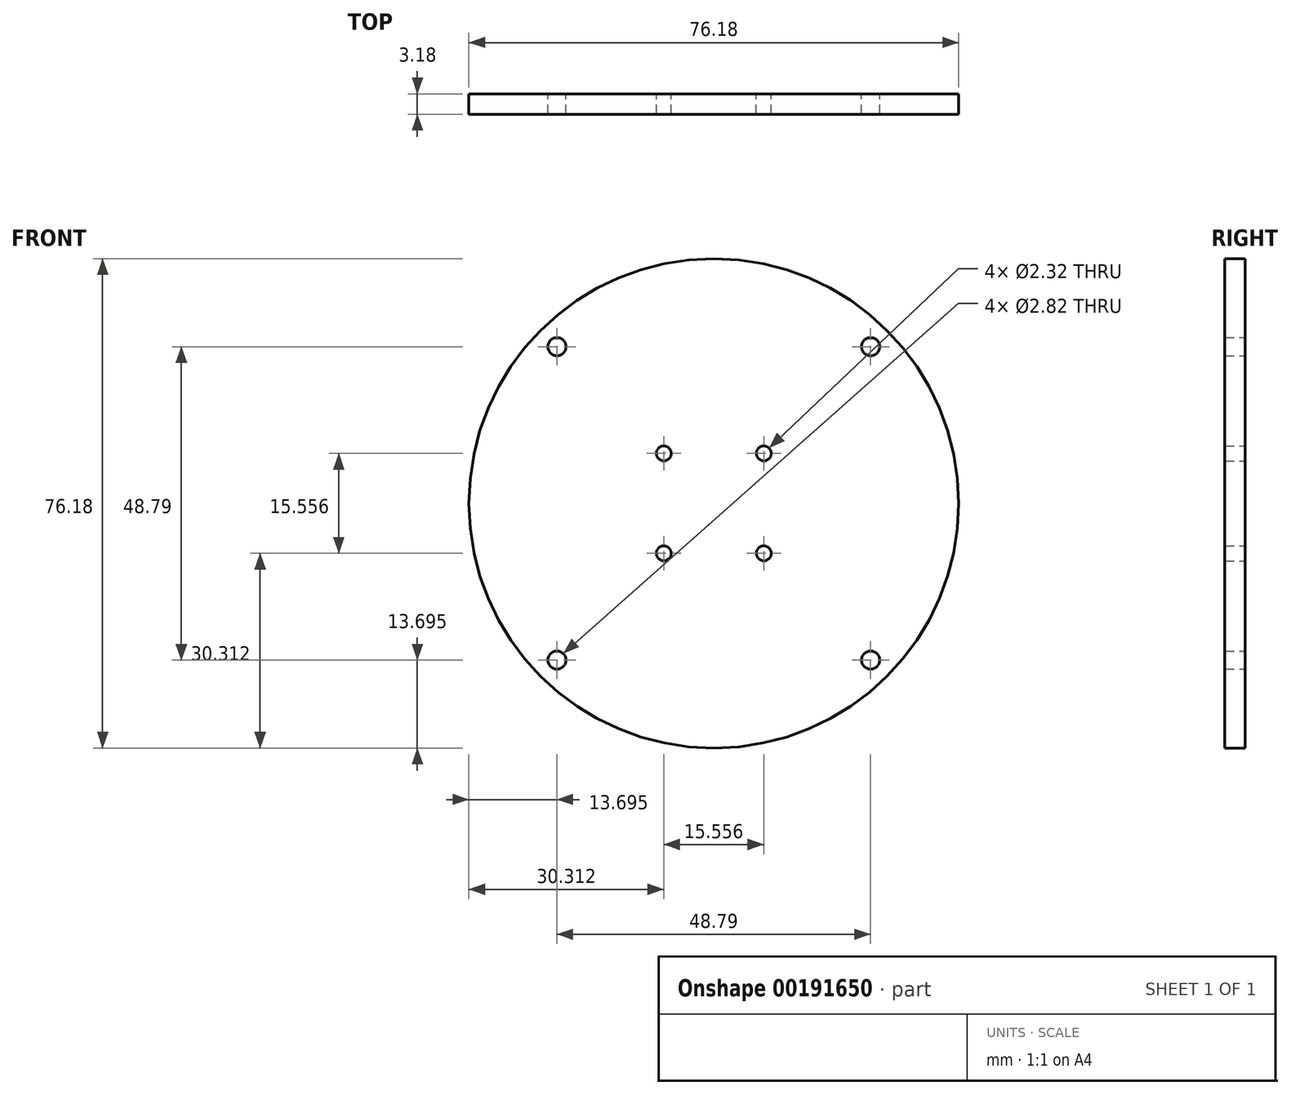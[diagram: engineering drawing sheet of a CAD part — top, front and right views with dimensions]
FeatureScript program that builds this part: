
annotation { "Feature Type Name" : "Feature", "Feature Type Description" : "" }
export const myFeature = defineFeature(function(context is Context, id is Id, definition is map)
    precondition{}
    {
        {
            var Q0;
            Q0=qCreatedBy(makeId("Front.planeOp"),FACE);
            var sketch = newSketch(context, id + "F0", { "sketchPlane" : qUnion([Q0])});
            skCircle(sketch, "E0", {"center": v(-24.4, -24.4) * mm, "radius": 1.41 * mm});
            skCircle(sketch, "E1", {"center": v(24.4, 24.4) * mm, "radius": 1.41 * mm});
            skCircle(sketch, "E2", {"center": v(7.78, -7.78) * mm, "radius": 1.16 * mm});
            skCircle(sketch, "E3", {"center": v(-7.78, -7.78) * mm, "radius": 1.16 * mm});
            skCircle(sketch, "E4", {"center": v(0, 0) * mm, "radius": 38.09 * mm});
            skCircle(sketch, "E5", {"center": v(7.78, 7.78) * mm, "radius": 1.16 * mm});
            skCircle(sketch, "E6", {"center": v(-7.78, 7.78) * mm, "radius": 1.16 * mm});
            skCircle(sketch, "E7", {"center": v(24.4, -24.4) * mm, "radius": 1.41 * mm});
            skCircle(sketch, "E8", {"center": v(-24.4, 24.4) * mm, "radius": 1.41 * mm});
            skCircle(sketch, "E9", {"center": v(0, 0) * mm, "radius": 11 * mm, "construction": true});
            skLineSegment(sketch, "E10", {"start": v(0, 0) * mm, "end": v(-30.06, 30.06) * mm, "construction": true});
            skLineSegment(sketch, "E11", {"start": v(0, 0) * mm, "end": v(28.77, 28.77) * mm, "construction": true});
            skLineSegment(sketch, "E12", {"start": v(0, 0) * mm, "end": v(30.97, -30.97) * mm, "construction": true});
            skLineSegment(sketch, "E13", {"start": v(0, 0) * mm, "end": v(-27.72, -27.72) * mm, "construction": true});
            skLineSegment(sketch, "E14", {"start": v(-19.93, 0) * mm, "end": v(19.38, 0) * mm, "construction": true});
            skSolve(sketch);
        }
        {
            var Q0;
            Q0 = qSketchRegion(id + "F0", true);
            extrude(context, id + "F1", {"entities" : qUnion([Q0]), "depth" : 3.17 * mm});
        }
    });
